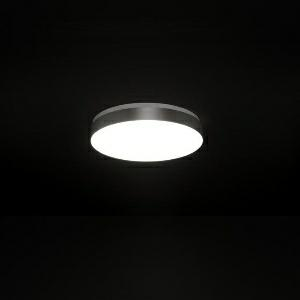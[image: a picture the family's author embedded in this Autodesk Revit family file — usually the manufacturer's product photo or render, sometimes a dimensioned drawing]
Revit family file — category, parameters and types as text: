
# Revit family: spectral_norea_norea-ra_416_4300_840_os_0182
name_source: partatom
category: Lighting Fixtures
revit_build: Autodesk Revit 2016 (Build: 20150220_1215(x64)
units: mm (PartAtom-declared; Revit-internal decimal feet)

## family parameters
Cut with Voids When Loaded = No
Host = Face
Light Source = No
Part Type = Normal
Room Calculation Point = No
Round Connector Dimension = Use Diameter
Shared = No

## types (1)
- SPECTRAL NOREA (1 x )
    Apparent Load = 0 VA
    Approval mark = CE
    CIE Flux Codes = 47 77 95 100 71
    Control Gear = Electronic transformer
    Default Elevation = 1800 mm
    Description = SPT0000019
NOREA surface-mounted luminaire

Design:
Round luminaire element comprising an acrylic opal glass panel in an anodised aluminium profile frame surround. The frame is fastened to the powder
coated steel body with a bayonet fixture with clip. The metal body accommodates the electrical components and electronic ballast. The LED module is formed as a round LED flat board and can be removed for installation or exchange using a key-hole screw connection. Plug-in electrical connection of the LED flat board. Luminaire with heat-resistant wiring Luminaire with heat-resistant wiring. Homogenous illumination of the light surface. Suitable for ceiling or wall mounting. Protection rating IP20, safety class I.

Colour:
Housing - similar to RAL 9016 white silk matt;
Frame - natural anodised
    Height = 80 mm  [stored 0.262467 ft]
    Lamp = 1 x
    Lamp count = 1
    Length = 416 mm
    Luminous efficacy = 0 lm/W
    Manufacturer = Ridi
    ModVariant = No
    Model = NOREA-RA 416/4300/840 OS
    Mounting Place = Ceiling
    Mounting Type = Surface mounted
    Number of Poles = 1
    OnlyDefault = Yes
    Power Factor = 1
    Product Name = SPECTRAL NOREA
    Product group = Ceiling mounted luminaire
    ProductGroupID = 3
    Protection Class = Protection class
    Protection Degree = IP 20
    RlxData = <blob elided: 29913 chars, md5=c13bd900>
    Socket = socket
    Standby Power = 0 W
    System Light Flux = 0 lm
    System Power = 0 W
    Type Image = rundmittel01_-_kopie.jpg
    URL = http://reluxnet.relux.com
    VarID = 1
    Voltage = 0 V
    Weight = 0.00 kg
    Width = 0 mm  [stored 0 ft]

note: [stored X ft] marks values corroborated as IEEE doubles in the binary element streams (Revit-internal decimal feet)

## geometry (parser evidence)
native form markers: Sweep x12
no freeform markers — native parametric forms only
